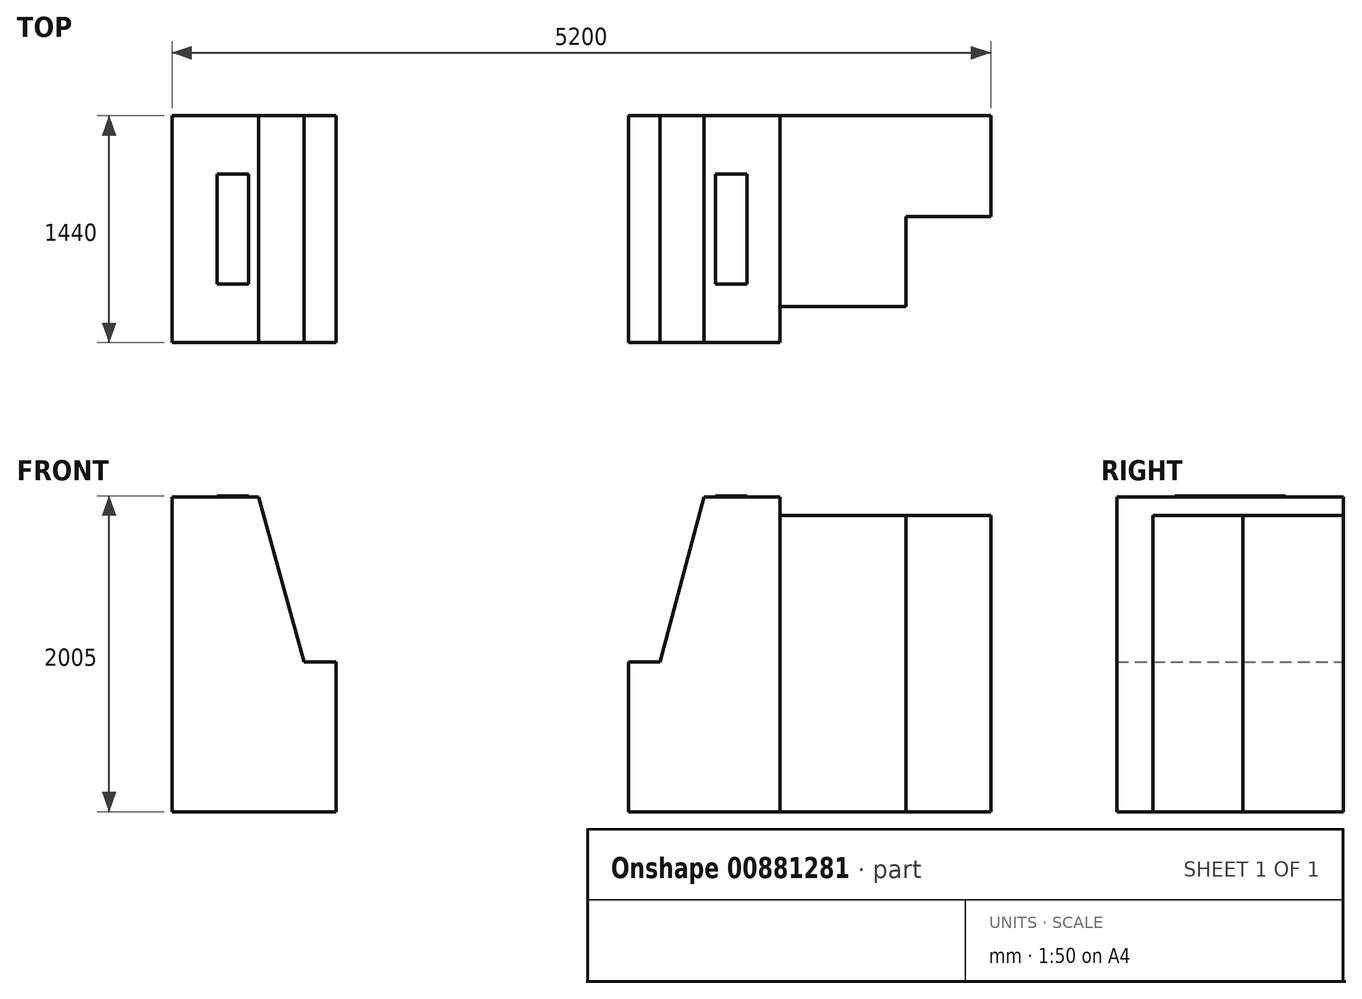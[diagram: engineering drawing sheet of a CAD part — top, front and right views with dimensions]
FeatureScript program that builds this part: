
annotation { "Feature Type Name" : "Feature", "Feature Type Description" : "" }
export const myFeature = defineFeature(function(context is Context, id is Id, definition is map)
    precondition{}
    {
        {
            var Q0;
            Q0=qCreatedBy(makeId("Front.planeOp"),FACE);
            var sketch = newSketch(context, id + "F0", { "sketchPlane" : qUnion([Q0])});
            skLineSegment(sketch, "E0.bottom", {"start": v(0, 0) * mm, "end": v(1040, 0) * mm});
            skLineSegment(sketch, "E0.top", {"start": v(0, 2000) * mm, "end": v(550, 2000) * mm});
            skLineSegment(sketch, "E0.left", {"start": v(0, 0) * mm, "end": v(0, 2000) * mm});
            skLineSegment(sketch, "E0.right", {"start": v(1040, 0) * mm, "end": v(1040, 950) * mm});
            skLineSegment(sketch, "E1", {"start": v(550, 2000) * mm, "end": v(840, 950) * mm});
            skLineSegment(sketch, "E2", {"start": v(840, 950) * mm, "end": v(1040, 950) * mm});
            skLineSegment(sketch, "E3.MirrorCS", {"start": v(3860, 2000) * mm, "end": v(3380, 2000) * mm});
            skLineSegment(sketch, "E4.MirrorCS", {"start": v(3380, 2000) * mm, "end": v(3100, 950) * mm});
            skLineSegment(sketch, "E5.MirrorCS", {"start": v(3100, 950) * mm, "end": v(2900, 950) * mm});
            skLineSegment(sketch, "E6.MirrorCS", {"start": v(2900, 0) * mm, "end": v(2900, 950) * mm});
            skLineSegment(sketch, "E7.MirrorCS", {"start": v(3860, 0) * mm, "end": v(2900, 0) * mm});
            skLineSegment(sketch, "E8.MirrorCS", {"start": v(3860, 0) * mm, "end": v(3860, 2000) * mm});
            skLineSegment(sketch, "E9", {"start": v(3860, 0) * mm, "end": v(5200, 0) * mm});
            skLineSegment(sketch, "E10", {"start": v(5200, 0) * mm, "end": v(5200, 1880) * mm});
            skLineSegment(sketch, "E11", {"start": v(5200, 1880) * mm, "end": v(3860, 1880) * mm});
            skSolve(sketch);
        }
        {
            var Q0;
            Q0=makeQuery(id+"F0.imprint","IMPRINT",FACE,{"disambiguationData":[TD([[makeQuery(id+"F0.imprint","IMPRINT",EDGE,{"derivedFrom":sQuery(id+"F0.wireOp",EDGE,"E0.bottom")}),1.0]])]});
            var Q1;
            {var subQ0=sQuery(id+"F0.wireOp",EDGE,"E3.MirrorCS");Q1=makeQuery(id+"F0.imprint","IMPRINT",FACE,{"disambiguationData":[TD([[makeQuery(id+"F0.imprint","IMPRINT",EDGE,{"derivedFrom":subQ0}),1.0]])]});}
            var Q2;
            {var subQ0=sQuery(id+"F0.wireOp",EDGE,"E9");Q2=makeQuery(id+"F0.imprint","IMPRINT",FACE,{"disambiguationData":[TD([[makeQuery(id+"F0.imprint","IMPRINT",EDGE,{"derivedFrom":subQ0}),1.0]])]});}
            extrude(context, id + "F1", {"entities" : qUnion([Q0, Q1, Q2]), "depth" : 1440 * mm, "offsetDistance" : 25 * mm});
        }
        {
            var Q0;
            Q0=makeQuery(id+"F1.opExtrude","SWEPT_FACE",FACE,{"disambiguationData":[OSD([sQuery(id+"F0.wireOp",EDGE,"E11")])]});
            var sketch = newSketch(context, id + "F2", { "sketchPlane" : qUnion([Q0])});
            skLineSegment(sketch, "E12", {"start": v(3860, -1440) * mm, "end": v(5200, -1440) * mm});
            skLineSegment(sketch, "E13", {"start": v(5200, -1440) * mm, "end": v(5200, -640) * mm});
            skLineSegment(sketch, "E14", {"start": v(5200, -640) * mm, "end": v(4660, -640) * mm});
            skLineSegment(sketch, "E15", {"start": v(4660, -640) * mm, "end": v(4660, -1210) * mm});
            skLineSegment(sketch, "E16", {"start": v(4660, -1210) * mm, "end": v(3860, -1210) * mm});
            skLineSegment(sketch, "E17", {"start": v(3860, -1210) * mm, "end": v(3860, -1440) * mm});
            skLineSegment(sketch, "E18", {"start": v(0, 0) * mm, "end": v(0, -1440) * mm});
            skSolve(sketch);
        }
        {
            var Q0;
            Q0 = qSketchRegion(id + "F2", true);
            extrude(context, id + "F3", {"entities" : qUnion([Q0]), "operationType" : NewBodyOperationType.REMOVE, "oppositeDirection" : true, "depth" : 2080 * mm, "offsetDistance" : 25 * mm});
        }
        {
            var Q0;
            Q0=makeQuery(id+"F1.opExtrude","SWEPT_FACE",FACE,{"disambiguationData":[OSD([sQuery(id+"F0.wireOp",EDGE,"E0.top")])]});
            var sketch = newSketch(context, id + "F4", { "sketchPlane" : qUnion([Q0])});
            skLineSegment(sketch, "E19", {"start": v(170.09, -720) * mm, "end": v(3647.6, -720) * mm, "construction": true});
            skPoint(sketch, "E19.startSnap0", {"position": v(0, -720) * mm});
            skLineSegment(sketch, "E20", {"start": v(385, -273.03) * mm, "end": v(385, -1135.15) * mm, "construction": true});
            skLineSegment(sketch, "E21", {"start": v(3550, -295.68) * mm, "end": v(3550, -1104.26) * mm, "construction": true});
            skLineSegment(sketch, "E22.bottom", {"start": v(485, -1070) * mm, "end": v(285, -1070) * mm});
            skLineSegment(sketch, "E22.top", {"start": v(485, -370) * mm, "end": v(285, -370) * mm});
            skLineSegment(sketch, "E22.left", {"start": v(485, -1070) * mm, "end": v(485, -370) * mm});
            skLineSegment(sketch, "E22.right", {"start": v(285, -1070) * mm, "end": v(285, -370) * mm});
            skPoint(sketch, "E22.middle", {"position": v(385, -720) * mm});
            skLineSegment(sketch, "E23.bottom", {"start": v(3650, -1070) * mm, "end": v(3450, -1070) * mm});
            skLineSegment(sketch, "E23.top", {"start": v(3650, -370) * mm, "end": v(3450, -370) * mm});
            skLineSegment(sketch, "E23.left", {"start": v(3650, -1070) * mm, "end": v(3650, -370) * mm});
            skLineSegment(sketch, "E23.right", {"start": v(3450, -1070) * mm, "end": v(3450, -370) * mm});
            skPoint(sketch, "E23.middle", {"position": v(3550, -720) * mm});
            skSolve(sketch);
        }
        {
            var Q0;
            Q0 = qSketchRegion(id + "F4", true);
            extrude(context, id + "F5", {"entities" : qUnion([Q0]), "depth" : 5 * mm, "offsetDistance" : 25 * mm});
        }
    });
